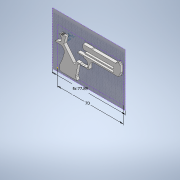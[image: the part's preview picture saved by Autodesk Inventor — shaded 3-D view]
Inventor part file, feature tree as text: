
AUTODESK INVENTOR PART (.ipt)
format: ipt  version: 2022 (Build 260153000, 153)  size: 3,213,824 bytes
history: native  units: in
note: dims shown in document units (in); Inventor stores cm internally (conversion verified against a paired STEP export)
features: other x9, sketch x7, reference x4, sheet_metal_op x3
ambient origin geometry x8: Origin, YZ Plane, XZ Plane, XY Plane, X Axis, Y Axis, Z Axis, Center Point
bodies: Body1 (feature_tree)
feature tree (23):
  sketch  "Sketch6"  dims[d94=3.0666in]
  sketch  "Sketch5"  dims[d93=0.2333in]
  sketch  "Sketch2"  dims[d25=2.7559in]
  sketch  "Sketch4"  dims[d87=0.2234in]
  sheet_metal_op  "Face4"
  sheet_metal_op  "Face5"
  other  "Image2"
  other  "Image4"
  other  "Image5"
  sketch  "Sketch7"  dims[d101=3.0666in]
  other  "Plate4"
  sketch  "Sketch8"  dims[d121=0.12in]
  other  "Plate5"
  sheet_metal_op  "Bend1"
  sketch  "Sketch9"  dims[d125=0.12in d126=0.12in d127=0.06in d128=0.24in d129=0.12in d130=0.12in d131=0.0in]
  reference  "Reference1"
  reference  "Reference2"
  reference  "Reference3"
  reference  "Reference4"
  other  "Cut1"
  parser-record x1  (decoder bookkeeping rows leaked as tree rows — omitted from the tree; the rows remain in map.json)
  other  "Assembly1.iam"
  other  "sheetmettaal:2"
note: 1 file-system path scrubbed to <path> (originals preserved in map.json)
